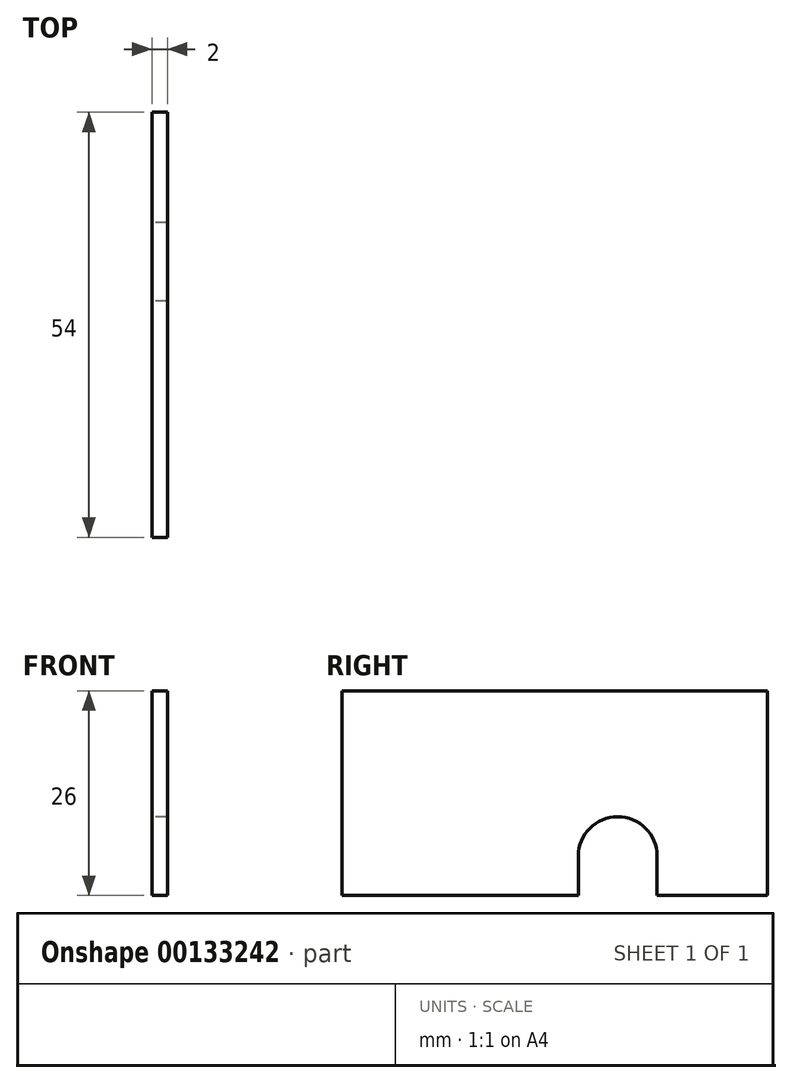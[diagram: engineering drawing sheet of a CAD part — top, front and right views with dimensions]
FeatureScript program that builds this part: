
annotation { "Feature Type Name" : "Feature", "Feature Type Description" : "" }
export const myFeature = defineFeature(function(context is Context, id is Id, definition is map)
    precondition{}
    {
        {
            var Q0;
            Q0=qCreatedBy(makeId("Right.planeOp"),FACE);
            var sketch = newSketch(context, id + "F0", { "sketchPlane" : qUnion([Q0])});
            skLineSegment(sketch, "E0.bottom", {"start": v(0, 0) * mm, "end": v(54, 0) * mm});
            skLineSegment(sketch, "E0.top", {"start": v(0, -26) * mm, "end": v(30, -26) * mm});
            skLineSegment(sketch, "E0.left", {"start": v(0, 0) * mm, "end": v(0, -26) * mm});
            skLineSegment(sketch, "E0.right", {"start": v(54, 0) * mm, "end": v(54, -26) * mm});
            skLineSegment(sketch, "E1.top", {"start": v(35, -16) * mm, "end": v(35, -16) * mm});
            skLineSegment(sketch, "E1.left", {"start": v(30, -26) * mm, "end": v(30, -21) * mm});
            skLineSegment(sketch, "E1.right", {"start": v(40, -26) * mm, "end": v(40, -21) * mm});
            skPoint(sketch, "E2.visualSharp", {"position": v(30, -16) * mm});
            skArc(sketch, "E2.filletArc", {"start": v(35, -16) * mm, "mid": v(31.46, -17.46) * mm, "end": v(30, -21) * mm});
            skPoint(sketch, "E3.visualSharp", {"position": v(40, -16) * mm});
            skArc(sketch, "E3.filletArc", {"start": v(40, -21) * mm, "mid": v(38.54, -17.46) * mm, "end": v(35, -16) * mm});
            skLineSegment(sketch, "E4.trimOffspring", {"start": v(40, -26) * mm, "end": v(54, -26) * mm});
            skSolve(sketch);
        }
        {
            var Q0;
            Q0=makeQuery(id+"F0.imprint","IMPRINT",FACE,{"disambiguationData":[TD([[makeQuery(id+"F0.imprint","IMPRINT",EDGE,{"derivedFrom":sQuery(id+"F0.wireOp",EDGE,"E0.bottom")}),-1.0]])]});
            extrude(context, id + "F1", {"entities" : qUnion([Q0]), "depth" : 2 * mm});
        }
    });
